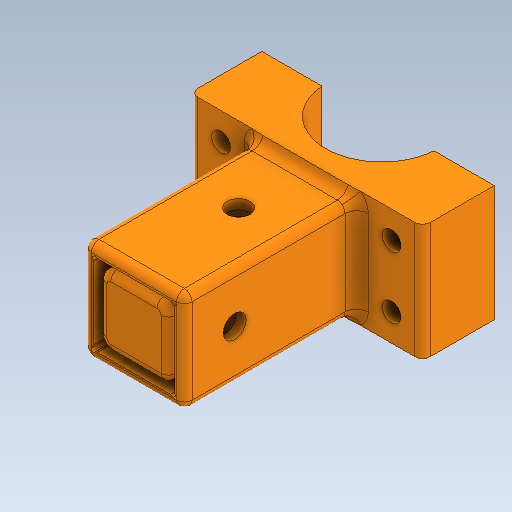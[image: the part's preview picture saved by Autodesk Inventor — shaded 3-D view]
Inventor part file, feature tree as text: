
AUTODESK INVENTOR PART (.ipt)
format: ipt  version: 2020.2 (Build 242310000, 310)  size: 365,056 bytes
history: native  units: mm
features: sketch x8, extrude x5, fillet x5, hole x3
ambient origin geometry x8: Origin, YZ Plane, XZ Plane, XY Plane, X Axis, Y Axis, Z Axis, Center Point
bodies: Solido1 (feature_tree)
feature tree (21):
  extrude  "Estrusione1"  Depth=18.0mm
  extrude  "Estrusione2"  Depth=40.0mm TaperAngle=0.0deg
  extrude  "Estrusione6"  Depth=26.0mm
  fillet  "Raccordo3"  Radius=26.0mm
  hole  "Foro8"  [1 undecoded]
  hole  "Foro9"  [1 undecoded]
  extrude  "Estrusione7"  Depth=3.0mm
  extrude  "Estrusione8"  Depth=21.0mm
  hole  "Foro10"  [1 undecoded]
  fillet  "Raccordo5"  Radius=40.0mm
  fillet  "Raccordo6"  Radius=2.0mm
  fillet  "Raccordo7"  Radius=13.0mm
  fillet  "Raccordo8"  [1 undecoded]
  sketch  "Schizzo1"
  sketch  "Schizzo2"
  sketch  "Schizzo12"
  sketch  "Schizzo13"
  sketch  "Schizzo14"
  sketch  "Schizzo17"
  sketch  "Schizzo18"
  sketch  "Schizzo19"
note: 4 required parameter values undecoded (feature->parameter linkage not recoverable at this tier; creation-order binding heuristic only, values carry confidence <= 0.55)
